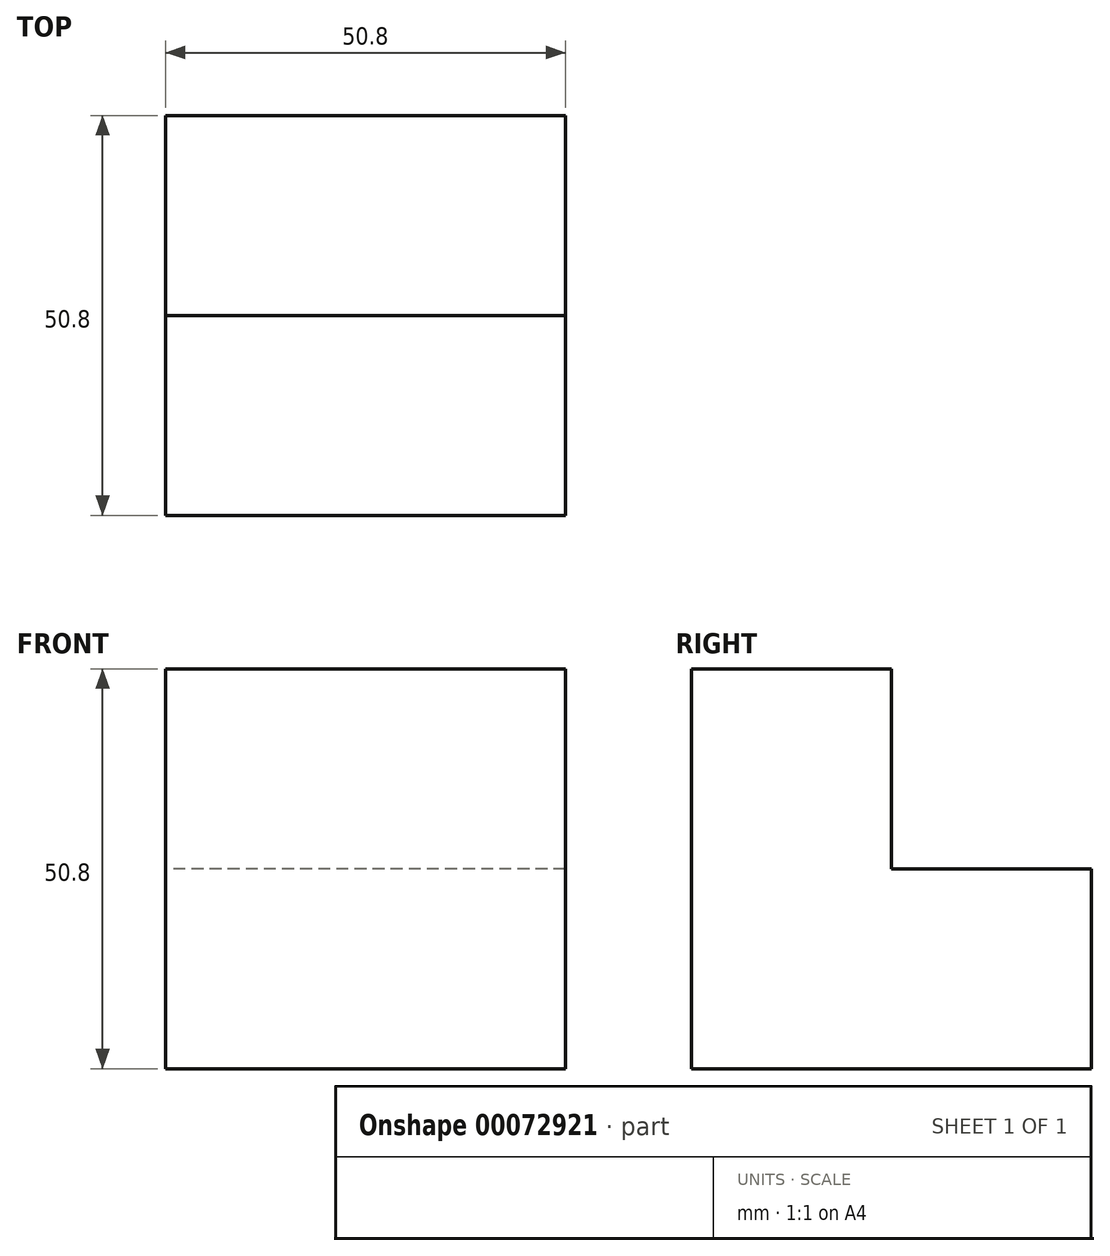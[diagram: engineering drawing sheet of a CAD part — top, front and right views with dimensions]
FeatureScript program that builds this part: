
annotation { "Feature Type Name" : "Feature", "Feature Type Description" : "" }
export const myFeature = defineFeature(function(context is Context, id is Id, definition is map)
    precondition{}
    {
        {
            var Q0;
            Q0=qCreatedBy(makeId("Right.planeOp"),FACE);
            var sketch = newSketch(context, id + "F0", { "sketchPlane" : qUnion([Q0])});
            skLineSegment(sketch, "E0", {"start": v(-49.2, 35.81) * mm, "end": v(-49.2, -14.99) * mm});
            skLineSegment(sketch, "E1", {"start": v(-49.2, -14.99) * mm, "end": v(1.6, -14.99) * mm});
            skLineSegment(sketch, "E2", {"start": v(1.6, -14.99) * mm, "end": v(1.6, 10.41) * mm});
            skLineSegment(sketch, "E3", {"start": v(1.6, 10.41) * mm, "end": v(-23.8, 10.41) * mm});
            skLineSegment(sketch, "E4", {"start": v(-23.8, 10.41) * mm, "end": v(-23.8, 35.81) * mm});
            skLineSegment(sketch, "E5", {"start": v(-23.8, 35.81) * mm, "end": v(-49.2, 35.81) * mm});
            skSolve(sketch);
        }
        {
            var Q0;
            Q0=makeQuery(id+"F0.imprint","IMPRINT",FACE,{"disambiguationData":[TD([[makeQuery(id+"F0.imprint","IMPRINT",EDGE,{"derivedFrom":sQuery(id+"F0.wireOp",EDGE,"E0")}),1.0]])]});
            extrude(context, id + "F1", {"entities" : qUnion([Q0]), "depth" : 25.4 * mm});
        }
        {
            var Q0;
            Q0=makeQuery(id+"F1.opExtrude","CAP_FACE",FACE,{"disambiguationData":[OSD([sQuery(id+"F0.wireOp",EDGE,"E0"),sQuery(id+"F0.wireOp",EDGE,"E1"),sQuery(id+"F0.wireOp",EDGE,"E2"),sQuery(id+"F0.wireOp",EDGE,"E3"),sQuery(id+"F0.wireOp",EDGE,"E4"),sQuery(id+"F0.wireOp",EDGE,"E5")])],"isStart":true});
            extrude(context, id + "F2", {"entities" : qUnion([Q0]), "operationType" : NewBodyOperationType.ADD, "depth" : 25.4 * mm});
        }
    });
